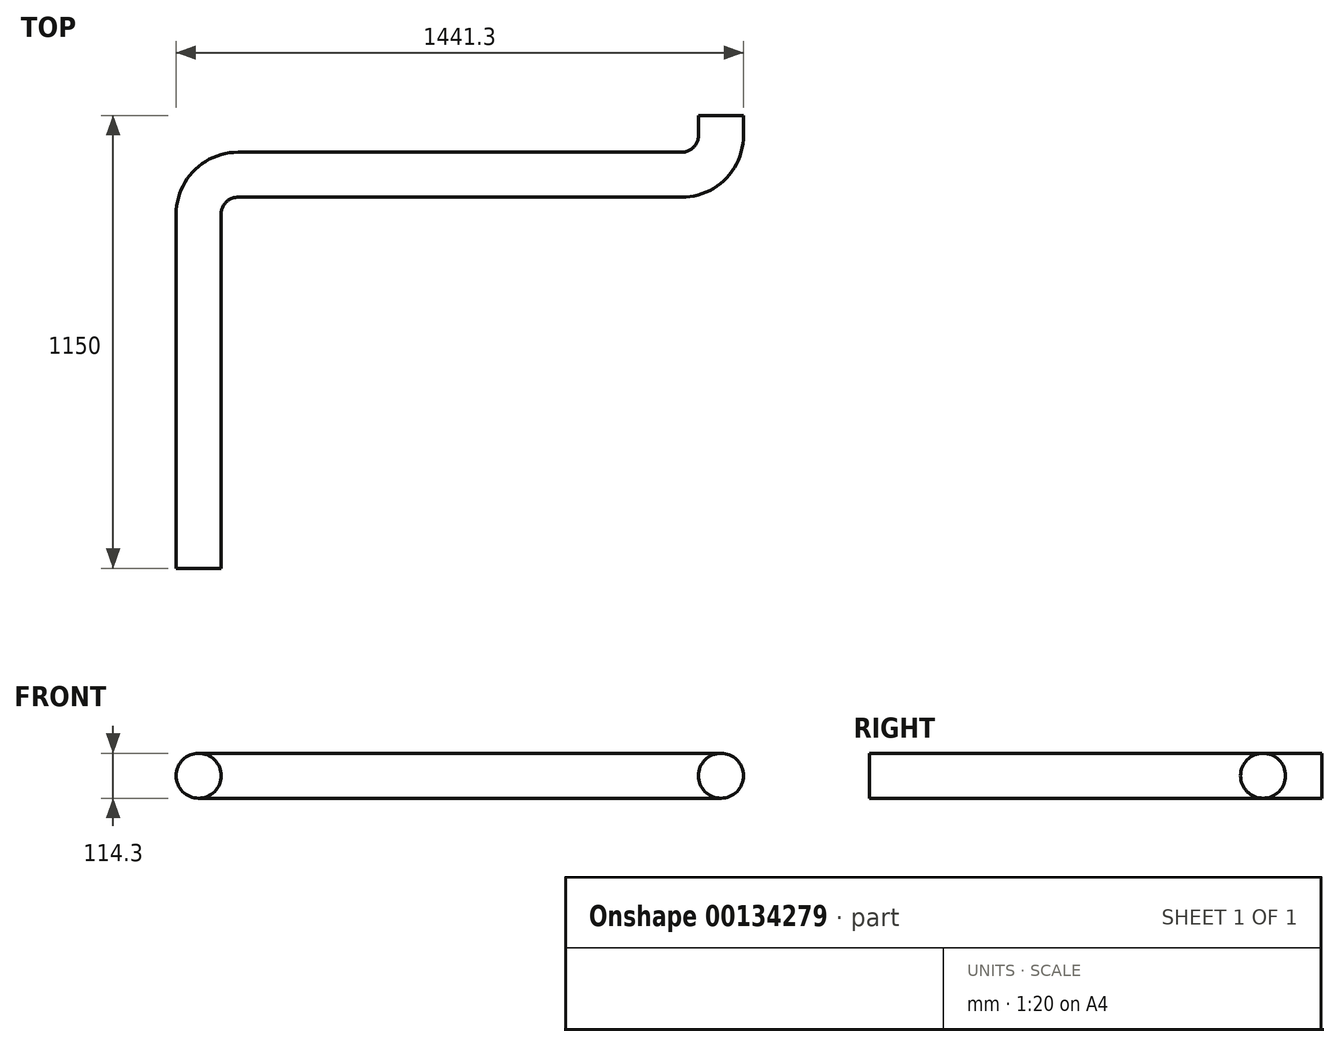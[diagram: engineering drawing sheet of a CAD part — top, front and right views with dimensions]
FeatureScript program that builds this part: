
annotation { "Feature Type Name" : "Feature", "Feature Type Description" : "" }
export const myFeature = defineFeature(function(context is Context, id is Id, definition is map)
    precondition{}
    {
        {
            var Q0;
            Q0=qCreatedBy(makeId("Front.planeOp"),FACE);
            var sketch = newSketch(context, id + "F0", { "sketchPlane" : qUnion([Q0])});
            skCircle(sketch, "E0", {"center": v(0, 0) * mm, "radius": 57.15 * mm});
            skSolve(sketch);
        }
        {
            var Q0;
            Q0=qCreatedBy(makeId("Top.planeOp"),FACE);
            var sketch = newSketch(context, id + "F1", { "sketchPlane" : qUnion([Q0])});
            skLineSegment(sketch, "E1", {"start": v(0, 0) * mm, "end": v(0, -50) * mm});
            skLineSegment(sketch, "E2", {"start": v(-100, -150) * mm, "end": v(-1227, -150) * mm});
            skLineSegment(sketch, "E3", {"start": v(-1327, -250) * mm, "end": v(-1327, -1150) * mm});
            skPoint(sketch, "E4.visualSharp", {"position": v(0, -150) * mm});
            skArc(sketch, "E4.filletArc", {"start": v(-100, -150) * mm, "mid": v(-29.29, -120.71) * mm, "end": v(0, -50) * mm});
            skPoint(sketch, "E5.visualSharp", {"position": v(-1327, -150) * mm});
            skArc(sketch, "E5.filletArc", {"start": v(-1227, -150) * mm, "mid": v(-1297.71, -179.29) * mm, "end": v(-1327, -250) * mm});
            skSolve(sketch);
        }
        {
            var Q0;
            Q0=makeQuery(id+"F0.imprint","IMPRINT",FACE,{"disambiguationData":[TD([[makeQuery(id+"F0.imprint","IMPRINT",EDGE,{"derivedFrom":sQuery(id+"F0.wireOp",EDGE,"E0")}),1.0]])]});
            var Q1;
            Q1 = qConstructionFilter(qBodyType(qCreatedBy(id + "F1" ,EDGE), BodyType.WIRE), ConstructionObject.NO);
            sweep(context, id + "F2", {"profiles" : qUnion([Q0]), "path" : qUnion([Q1])});
        }
    });
